# Revit family: Faucet-Wall_Mount-Lavatory-KOHLER-PURIST-K-14415A
name_source: partatom
category: Plumbing Fixtures
revit_build: Autodesk Revit 2017 (Build: 20160225_1515(x64)
units: mm (PartAtom-declared; Revit-internal decimal feet)

## family parameters
Cut with Voids When Loaded = No
Host = Face
OmniClass Number = 23.31.11.00
OmniClass Title = Faucets
Part Type = Normal
Room Calculation Point = No
Round Connector Dimension = Use Diameter
Shared = No

## types (6) — shared parameters
ADA Compliant = No
Assembly Code = D2010
CW Connection = Yes
Cold Water Inlet = Cold Water Inlet
Date Modified = 08/21/2020
Default Elevation = 36"
Description = BASIN SET WALL MOUNT 210MM SPOUT
Drain Included = No
Flow Rate = 2 GPM
HW Connection = Yes
Handle Clearance = 2 3/16"
Handle Height = 3 1/2"
Height = 2"
Hot Water Inlet = Hot Water Inlet
Length = 8 1/4"
Manufacturer = KOHLER Co.
Master Format 2014 = 22 41 39
Master Format 2014 Name = Residential Faucets, Supplies, and Trim
Material = Solid Brass Construction
Pressure = 60.00 psi
Product Name = PURIST
Spout Reach = 8 1/4"
URL = https://www.kohlerasiapacific.com
Vent Connection = No
Waste Connection = No
Waste Water Outlet = Waste Water Outlet
WaterSense Certified = No

## per-type parameters (varying)
| type | Finish | Model | Type |
| 2.2 GPM, CP-Polished Chrome | Kohler-Metal-CP-Polished_Chrome | K-14415A-4-CP | 1 |
| 1.85 GPM, CP-Polished Chrome | Kohler-Metal-CP-Polished_Chrome | K-14415A-B4-CP | 2 |
| 1.85 GPM, BN-Vibrant Brushed Nickel | Kohler-Metal-BN-Vibrant_Brushed_Nickel | K-14415A-B4-BN | 3 |
| 1.85 GPM, BV-Brushed Bronze | Kohler-Metal-BV-Brushed_Bronze | K-14415A-B4-BV | 4 |
| 1.85 GPM, RGD-Polished Rose Gold | Kohler-Metal-RGD-Polished_Rose_Gold | K-14415A-B4-RGD | 5 |
| 1.85 GPM, PGD-Modern Polished Gold | Kohler-Metal-PGD-Modern_Polished_Gold | K-14415A-B4-PGD | 6 |

## geometry (parser evidence)
native form markers: Sweep x10
no freeform markers — native parametric forms only
